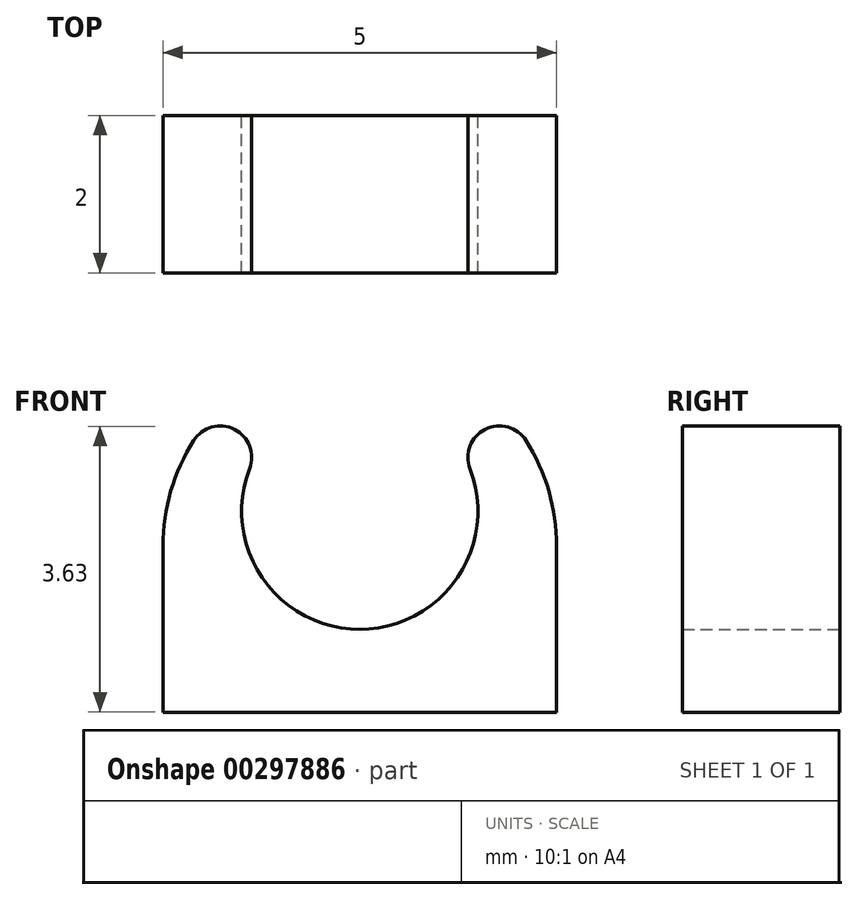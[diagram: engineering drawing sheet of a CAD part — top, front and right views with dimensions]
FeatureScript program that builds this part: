
annotation { "Feature Type Name" : "Feature", "Feature Type Description" : "" }
export const myFeature = defineFeature(function(context is Context, id is Id, definition is map)
    precondition{}
    {
        {
            var Q0;
            Q0=qCreatedBy(makeId("Front.planeOp"),FACE);
            var sketch = newSketch(context, id + "F0", { "sketchPlane" : qUnion([Q0])});
            skArc(sketch, "E0", {"start": v(-2.11, 1.34) * mm, "mid": v(-2.4, 0.7) * mm, "end": v(-2.5, 0) * mm});
            skArc(sketch, "E1", {"start": v(-1.4, 0.98) * mm, "mid": v(0, -1.06) * mm, "end": v(1.4, 0.98) * mm});
            skLineSegment(sketch, "E2.bottom", {"start": v(2.5, 0) * mm, "end": v(1.43, 0) * mm});
            skLineSegment(sketch, "E2.top", {"start": v(2.5, -2.11) * mm, "end": v(-2.5, -2.11) * mm});
            skLineSegment(sketch, "E2.left", {"start": v(2.5, 0) * mm, "end": v(2.5, -2.11) * mm});
            skLineSegment(sketch, "E2.right", {"start": v(-2.5, 0) * mm, "end": v(-2.5, -2.11) * mm});
            skPoint(sketch, "E2.middle", {"position": v(0, -1.06) * mm});
            skArc(sketch, "E3.trimOffspring", {"start": v(2.5, 0) * mm, "mid": v(2.4, 0.7) * mm, "end": v(2.11, 1.34) * mm});
            skLineSegment(sketch, "E4.trimOffspring", {"start": v(-1.43, 0) * mm, "end": v(-2.5, 0) * mm});
            skArc(sketch, "E5", {"start": v(-1.4, 0.98) * mm, "mid": v(-1.6, 1.48) * mm, "end": v(-2.11, 1.34) * mm});
            skArc(sketch, "E6.MirrorCS", {"start": v(1.4, 0.98) * mm, "mid": v(1.6, 1.48) * mm, "end": v(2.11, 1.34) * mm});
            skSolve(sketch);
        }
        {
            var Q0;
            Q0 = qSketchRegion(id + "F0", true);
            extrude(context, id + "F1", {"entities" : qUnion([Q0]), "depth" : 2 * mm});
        }
    });
